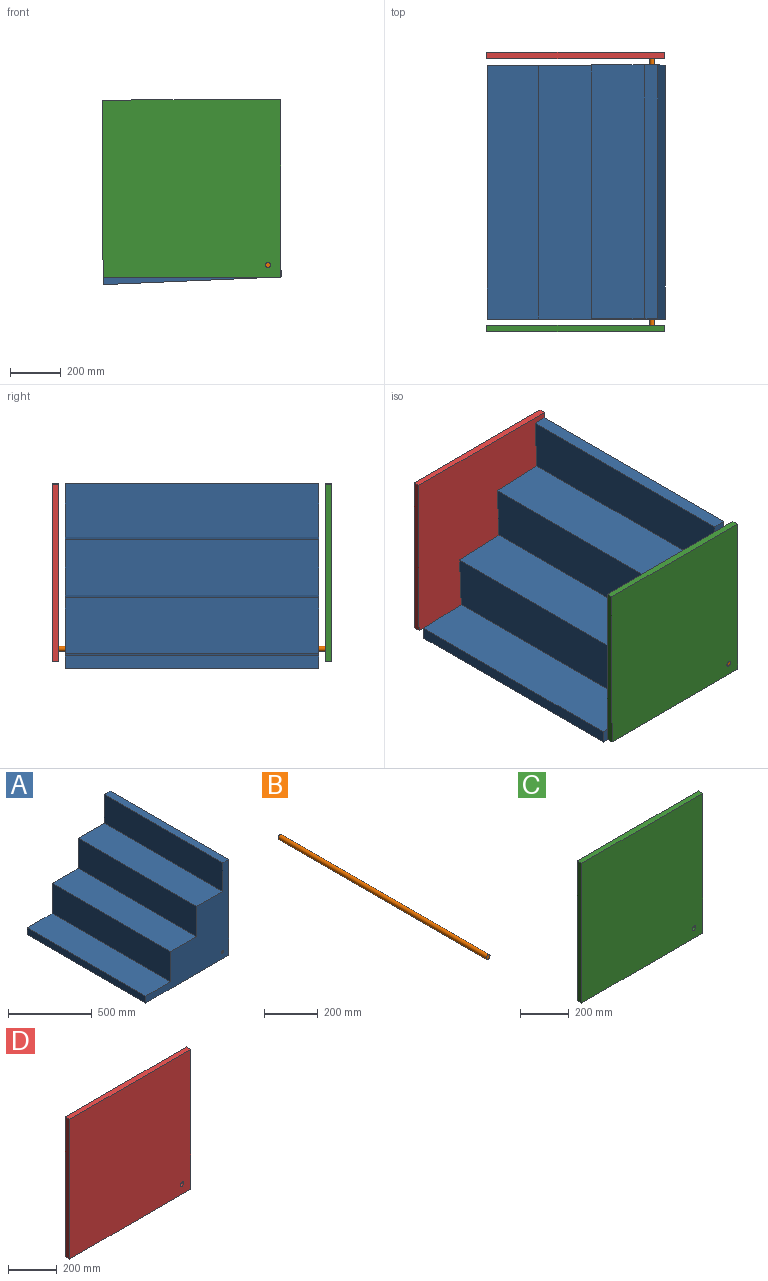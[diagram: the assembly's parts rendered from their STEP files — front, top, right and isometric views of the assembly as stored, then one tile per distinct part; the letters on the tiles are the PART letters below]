
ASSEMBLY  parts=4 mates=3
PART A: 13 faces, bbox 700x1000x700 mm
  f0: plane 1000x220mm, normal (0,0,1), area 220000mm2, adj f1,f2,f9,f10
  f1: plane 1000x220mm, normal (-1,0,0), area 220000mm2, adj f0,f9,f10,f12
  f2: plane 1000x210mm, normal (-1,0,0), area 210000mm2, adj f0,f6,f9,f10
  f3: plane 1000x50mm, normal (-1,0,0), area 50000mm2, adj f4,f5,f9,f10
  f4: plane 1000x210mm, normal (0,0,1), area 210000mm2, adj f3,f9,f10,f11
  f5: plane 1000x700mm, normal (0,0,-1), area 700000mm2, adj f3,f7,f9,f10
  f6: plane 1000x50mm, normal (0,0,1), area 50000mm2, adj f2,f7,f9,f10
  f7: plane 1000x700mm, normal (1,0,0), area 700000mm2, adj f5,f6,f9,f10
  f8: cylinder r=10mm len=1000mm, axis (0,-1,0), area 62831.9mm2, adj f9,f10
  f9: plane 700x700mm, normal (0,1,0), area 212385.8mm2, adj f0,f1,f2,f3,f4,f5,f6,f7
  f10: plane 700x700mm, normal (0,-1,0), area 212385.8mm2, adj f0,f1,f2,f3,f4,f5,f6,f7
  f11: plane 1000x220mm, normal (-1,0,0), area 220000mm2, adj f4,f9,f10,f12
  f12: plane 1000x220mm, normal (0,0,1), area 220000mm2, adj f1,f9,f10,f11
PART B: 3 faces, bbox 20x1100x20 mm
  f0: plane 20x20mm, normal (0,1,0), area 314.2mm2, adj f2
  f1: plane 20x20mm, normal (0,-1,0), area 314.2mm2, adj f2
  f2: cylinder r=10mm len=1100mm, axis (0,-1,0), area 69115mm2, adj f0,f1
PART C: 7 faces, bbox 700x25x700 mm
  f0: plane 700x25mm, normal (-1,0,0), area 17500mm2, adj f2,f3,f5,f6
  f1: cylinder r=10mm len=25mm, axis (0,1,0), area 1570.8mm2, adj f5,f6
  f2: plane 700x25mm, normal (0,0,1), area 17500mm2, adj f0,f4,f5,f6
  f3: plane 700x25mm, normal (0,0,-1), area 17500mm2, adj f0,f4,f5,f6
  f4: plane 700x25mm, normal (1,0,0), area 17500mm2, adj f2,f3,f5,f6
  f5: plane 700x700mm, normal (0,1,0), area 489685.8mm2, adj f0,f1,f2,f3,f4
  f6: plane 700x700mm, normal (0,-1,0), area 489685.8mm2, adj f0,f1,f2,f3,f4
PART D: 7 faces, bbox 700x25x700 mm
  f0: plane 700x25mm, normal (1,0,0), area 17500mm2, adj f2,f3,f5,f6
  f1: cylinder r=10mm len=25mm, axis (0,-1,0), area 1570.8mm2, adj f5,f6
  f2: plane 700x25mm, normal (0,0,1), area 17500mm2, adj f0,f4,f5,f6
  f3: plane 700x25mm, normal (0,0,-1), area 17500mm2, adj f0,f4,f5,f6
  f4: plane 700x25mm, normal (-1,0,0), area 17500mm2, adj f2,f3,f5,f6
  f5: plane 700x700mm, normal (0,1,0), area 489685.8mm2, adj f0,f1,f2,f3,f4
  f6: plane 700x700mm, normal (0,-1,0), area 489685.8mm2, adj f0,f1,f2,f3,f4
PLACE A rot(axis=(0,-1,0),2.5deg) t=(121.58,-818.75,-179.99)mm
PLACE B rot(axis=(0,-1,0),90.1deg) t=(-885.14,-818.75,303.34)mm
PLACE C rot(axis=(0,-1,0),0.1deg) t=(132.69,-818.75,-211.62)mm fixed
PLACE D rot(axis=(0,-1,0),0.1deg) t=(132.69,-818.75,-211.62)mm fixed
MATE revolute B.f2 <-> C.f1  axis (0,-1,0) through (-633.7,-1868.75,-463.06)mm
MATE revolute B.f2 <-> A.f8  axis (0,-1,0) through (-633.7,-1318.75,-463.06)mm
MATE revolute D.f1 <-> B.f2  axis (0,1,0) through (-633.7,-768.75,-463.06)mm
